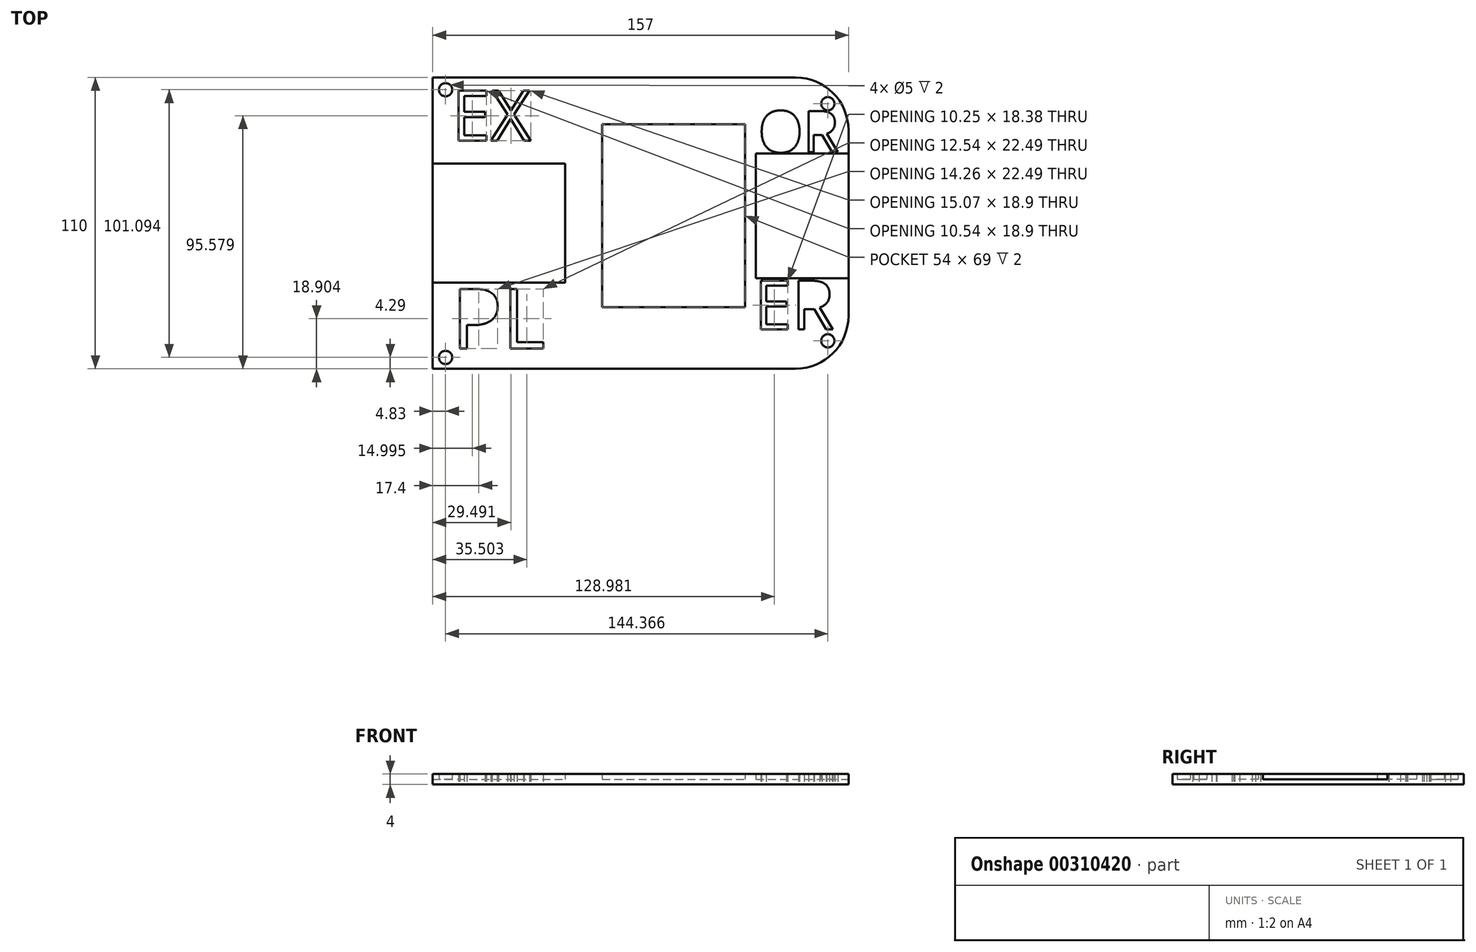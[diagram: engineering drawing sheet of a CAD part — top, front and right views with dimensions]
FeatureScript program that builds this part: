
annotation { "Feature Type Name" : "Feature", "Feature Type Description" : "" }
export const myFeature = defineFeature(function(context is Context, id is Id, definition is map)
    precondition{}
    {
        {
            var Q0;
            Q0=qCreatedBy(makeId("Front.planeOp"),FACE);
            var sketch = newSketch(context, id + "F0", { "sketchPlane" : qUnion([Q0])});
            skLineSegment(sketch, "E0.bottom", {"start": v(-78.5, 2) * mm, "end": v(78.5, 2) * mm});
            skLineSegment(sketch, "E0.top", {"start": v(-78.5, -2) * mm, "end": v(78.5, -2) * mm});
            skLineSegment(sketch, "E0.left", {"start": v(-78.5, 2) * mm, "end": v(-78.5, -2) * mm});
            skLineSegment(sketch, "E0.right", {"start": v(78.5, 2) * mm, "end": v(78.5, -2) * mm});
            skPoint(sketch, "E0.middle", {"position": v(0, 0) * mm});
            skSolve(sketch);
        }
        {
            var Q0;
            Q0 = qSketchRegion(id + "F0", true);
            extrude(context, id + "F1", {"entities" : qUnion([Q0]), "depth" : 110 * mm});
        }
        {
            var Q0;
            Q0=qCreatedBy(makeId("Top.planeOp"),FACE);
            var sketch = newSketch(context, id + "F2", { "sketchPlane" : qUnion([Q0])});
            skLineSegment(sketch, "E1.bottom", {"start": v(-81.5, -32.5) * mm, "end": v(-28.5, -32.5) * mm});
            skLineSegment(sketch, "E1.top", {"start": v(-81.5, -77.5) * mm, "end": v(-28.5, -77.5) * mm});
            skLineSegment(sketch, "E1.left", {"start": v(-81.5, -32.5) * mm, "end": v(-81.5, -77.5) * mm});
            skLineSegment(sketch, "E1.right", {"start": v(-28.5, -32.5) * mm, "end": v(-28.5, -77.5) * mm});
            skLineSegment(sketch, "E2.bottom", {"start": v(-14.54, -17.7) * mm, "end": v(39.46, -17.7) * mm});
            skLineSegment(sketch, "E2.top", {"start": v(-14.54, -86.7) * mm, "end": v(39.46, -86.7) * mm});
            skLineSegment(sketch, "E2.left", {"start": v(-14.54, -17.7) * mm, "end": v(-14.54, -86.7) * mm});
            skLineSegment(sketch, "E2.right", {"start": v(39.46, -17.7) * mm, "end": v(39.46, -86.7) * mm});
            skLineSegment(sketch, "E3.bottom", {"start": v(43.5, -28.76) * mm, "end": v(81.5, -28.76) * mm});
            skLineSegment(sketch, "E3.top", {"start": v(43.5, -75.76) * mm, "end": v(81.5, -75.76) * mm});
            skLineSegment(sketch, "E3.left", {"start": v(43.5, -28.76) * mm, "end": v(43.5, -75.76) * mm});
            skLineSegment(sketch, "E3.right", {"start": v(81.5, -28.76) * mm, "end": v(81.5, -75.76) * mm});
            skSolve(sketch);
        }
        {
            var Q0;
            Q0 = qSketchRegion(id + "F2", true);
            extrude(context, id + "F3", {"entities" : qUnion([Q0]), "operationType" : NewBodyOperationType.ADD, "depth" : 4 * mm});
        }
        {
            var Q0;
            Q0=makeQuery(id+"F1.opExtrude","CAP_EDGE",EDGE,{"disambiguationData":[OSD([sQuery(id+"F0.wireOp",EDGE,"E0.right")])],"isStart":false});
            fillet(context, id + "F4", {"entities" : qUnion([Q0]), "radius" : 20 * mm, "tangentPropagation" : true, "allowEdgeOverflow" : false});
        }
        {
            var Q0;
            Q0=makeQuery(id+"F1.opExtrude","CAP_EDGE",EDGE,{"disambiguationData":[OSD([sQuery(id+"F0.wireOp",EDGE,"E0.right")])],"isStart":true});
            fillet(context, id + "F5", {"entities" : qUnion([Q0]), "radius" : 20 * mm, "tangentPropagation" : true, "allowEdgeOverflow" : false});
        }
        {
            var Q0;
            Q0 = qSketchRegion(id + "F2", true);
            extrude(context, id + "F6", {"entities" : qUnion([Q0]), "operationType" : NewBodyOperationType.REMOVE, "depth" : 25 * mm});
        }
        {
            var Q0;
            Q0=qCreatedBy(makeId("Top.planeOp"),FACE);
            var sketch = newSketch(context, id + "F7", { "sketchPlane" : qUnion([Q0])});
            skCircle(sketch, "E4", {"center": v(-73.67, -4.62) * mm, "radius": 2.5 * mm});
            skCircle(sketch, "E5", {"center": v(70.7, -9.9) * mm, "radius": 2.5 * mm});
            skCircle(sketch, "E6", {"center": v(-73.67, -105.71) * mm, "radius": 2.5 * mm});
            skCircle(sketch, "E7", {"center": v(70.7, -99.44) * mm, "radius": 2.5 * mm});
            skSolve(sketch);
        }
        {
            var Q0;
            Q0 = qSketchRegion(id + "F7", true);
            extrude(context, id + "F8", {"entities" : qUnion([Q0]), "operationType" : NewBodyOperationType.REMOVE, "endBound" : BoundingType.THROUGH_ALL, "depth" : 70 * mm});
        }
        {
            var Q0;
            Q0=qCreatedBy(makeId("Top.planeOp"),FACE);
            var sketch = newSketch(context, id + "F9", { "sketchPlane" : qUnion([Q0])});
            skText(sketch, "E8", { "text": "EX", "fontName": "OpenSans-Regular.ttf"});
            skText(sketch, "E9", { "text": "PL", "fontName": "OpenSans-Regular.ttf"});
            skText(sketch, "E10", { "text": "OR", "fontName": "OpenSans-Regular.ttf"});
            skText(sketch, "E11", { "text": "ER", "fontName": "OpenSans-Regular.ttf"});
            const initialGuessF9  = {"E8": [-0.07137, -0.02387, 1, 0, 0.01906], "E9": [-0.07132, -0.10234, 1, 0, 0.02268], "E10": [0.04438, -0.02823, 1, 0, 0.0157], "E11": [0.04283, -0.09513, 1, 0, 0.01854]};
            skSetInitialGuess(sketch, initialGuessF9);
            skSolve(sketch);
        }
        {
            var Q0;
            Q0 = qSketchRegion(id + "F9", true);
            extrude(context, id + "F10", {"entities" : qUnion([Q0]), "operationType" : NewBodyOperationType.ADD, "endBound" : BoundingType.SYMMETRIC, "depth" : 25 * mm, "offsetDistance" : 25 * mm});
        }
        {
            var Q0;
            Q0 = qSketchRegion(id + "F9", true);
            extrude(context, id + "F11", {"entities" : qUnion([Q0]), "operationType" : NewBodyOperationType.REMOVE, "endBound" : BoundingType.SYMMETRIC, "depth" : 40 * mm, "offsetDistance" : 25 * mm});
        }
        {
            var Q0;
            Q0=makeQuery(id+"F10.boolean.opBoolean","SPLIT",FACE,{"disambiguationData":[TD([makeQuery(id+"F10.opExtrude","SWEPT_FACE",FACE,{"disambiguationData":[OSD([sQuery(id+"F9.wireOp",EDGE,"E11.sketch_text.stroke-23")])]})])],"derivedFrom":makeQuery(id+"F1.opExtrude","SWEPT_FACE",FACE,{"disambiguationData":[OSD([sQuery(id+"F0.wireOp",EDGE,"E0.bottom")])]})});
            var Q1;
            Q1=makeQuery(id+"F10.boolean.opBoolean","SPLIT",FACE,{"disambiguationData":[TD([makeQuery(id+"F10.opExtrude","SWEPT_FACE",FACE,{"disambiguationData":[OSD([sQuery(id+"F9.wireOp",EDGE,"E11.sketch_text.stroke-23")])]})])],"derivedFrom":makeQuery(id+"F1.opExtrude","SWEPT_FACE",FACE,{"disambiguationData":[OSD([sQuery(id+"F0.wireOp",EDGE,"E0.top")])]})});
            extrude(context, id + "F12", {"entities" : qUnion([Q0, Q1]), "operationType" : NewBodyOperationType.REMOVE, "endBound" : BoundingType.SYMMETRIC, "oppositeDirection" : true, "depth" : 25 * mm, "offsetDistance" : 25 * mm});
        }
        {
            var Q0;
            Q0=makeQuery(id+"F10.boolean.opBoolean","SPLIT",FACE,{"disambiguationData":[TD([makeQuery(id+"F10.opExtrude","SWEPT_FACE",FACE,{"disambiguationData":[OSD([sQuery(id+"F9.wireOp",EDGE,"E10.sketch_text.stroke-8")])]})])],"derivedFrom":makeQuery(id+"F1.opExtrude","SWEPT_FACE",FACE,{"disambiguationData":[OSD([sQuery(id+"F0.wireOp",EDGE,"E0.bottom")])]})});
            var Q1;
            Q1=makeQuery(id+"F10.boolean.opBoolean","SPLIT",FACE,{"disambiguationData":[TD([makeQuery(id+"F10.opExtrude","SWEPT_FACE",FACE,{"disambiguationData":[OSD([sQuery(id+"F9.wireOp",EDGE,"E10.sketch_text.stroke-8")])]})])],"derivedFrom":makeQuery(id+"F1.opExtrude","SWEPT_FACE",FACE,{"disambiguationData":[OSD([sQuery(id+"F0.wireOp",EDGE,"E0.top")])]})});
            extrude(context, id + "F13", {"entities" : qUnion([Q0, Q1]), "operationType" : NewBodyOperationType.REMOVE, "endBound" : BoundingType.SYMMETRIC, "oppositeDirection" : true, "depth" : 25 * mm, "offsetDistance" : 25 * mm});
        }
        {
            var Q0;
            Q0=makeQuery(id+"F10.boolean.opBoolean","SPLIT",FACE,{"disambiguationData":[TD([makeQuery(id+"F10.opExtrude","SWEPT_FACE",FACE,{"disambiguationData":[OSD([sQuery(id+"F9.wireOp",EDGE,"E9.sketch_text.stroke-8")])]})])],"derivedFrom":makeQuery(id+"F1.opExtrude","SWEPT_FACE",FACE,{"disambiguationData":[OSD([sQuery(id+"F0.wireOp",EDGE,"E0.bottom")])]})});
            var Q1;
            Q1=makeQuery(id+"F10.boolean.opBoolean","SPLIT",FACE,{"disambiguationData":[TD([makeQuery(id+"F10.opExtrude","SWEPT_FACE",FACE,{"disambiguationData":[OSD([sQuery(id+"F9.wireOp",EDGE,"E9.sketch_text.stroke-8")])]})])],"derivedFrom":makeQuery(id+"F1.opExtrude","SWEPT_FACE",FACE,{"disambiguationData":[OSD([sQuery(id+"F0.wireOp",EDGE,"E0.top")])]})});
            extrude(context, id + "F14", {"entities" : qUnion([Q0, Q1]), "operationType" : NewBodyOperationType.REMOVE, "endBound" : BoundingType.SYMMETRIC, "oppositeDirection" : true, "depth" : 25 * mm, "offsetDistance" : 25 * mm});
        }
        {
            var Q0;
            Q0=makeQuery(id+"F10.boolean.opBoolean","SPLIT",FACE,{"disambiguationData":[TD([makeQuery(id+"F10.opExtrude","SWEPT_FACE",FACE,{"disambiguationData":[OSD([sQuery(id+"F9.wireOp",EDGE,"E10.sketch_text.stroke-27")])]})])],"derivedFrom":makeQuery(id+"F1.opExtrude","SWEPT_FACE",FACE,{"disambiguationData":[OSD([sQuery(id+"F0.wireOp",EDGE,"E0.bottom")])]})});
            var Q1;
            Q1=makeQuery(id+"F10.boolean.opBoolean","SPLIT",FACE,{"disambiguationData":[TD([makeQuery(id+"F10.opExtrude","SWEPT_FACE",FACE,{"disambiguationData":[OSD([sQuery(id+"F9.wireOp",EDGE,"E10.sketch_text.stroke-27")])]})])],"derivedFrom":makeQuery(id+"F1.opExtrude","SWEPT_FACE",FACE,{"disambiguationData":[OSD([sQuery(id+"F0.wireOp",EDGE,"E0.top")])]})});
            extrude(context, id + "F15", {"entities" : qUnion([Q0, Q1]), "operationType" : NewBodyOperationType.REMOVE, "endBound" : BoundingType.SYMMETRIC, "oppositeDirection" : true, "depth" : 25 * mm, "offsetDistance" : 25 * mm});
        }
    });
